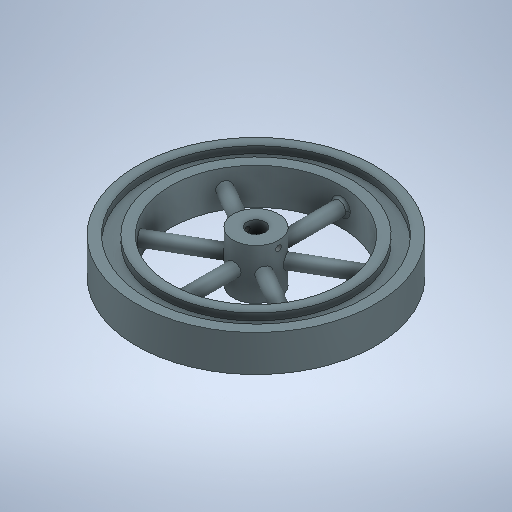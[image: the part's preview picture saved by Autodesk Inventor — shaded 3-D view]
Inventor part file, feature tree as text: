
AUTODESK INVENTOR PART (.ipt)
format: ipt  version: 2025.1 (Build 291241000, 241)  size: 387,072 bytes
history: native  units: mm
features: sketch x7, extrude x5, plane x3, hole x2, mirror x1, fillet x1, pattern_circular x1
ambient origin geometry x8: Origin, YZ Plane, XZ Plane, XY Plane, X Axis, Y Axis, Z Axis, Center Point
bodies: Solid1 (feature_tree)
feature tree (20):
  extrude  "Extrusion1"  Depth=16.0mm TaperAngle=0.0deg
  extrude  "Extrusion2"  Depth=16.0mm TaperAngle=0.0deg
  extrude  "Extrusion3"  Depth=96.0mm
  plane  "Work Plane1"
  mirror  "Mirror1"
  extrude  "Extrusion4"  TaperAngle=0.0deg  [1 undecoded]
  plane  "Work Plane2"
  extrude  "Extrusion5"  Depth=9.5mm TaperAngle=0.0deg
  fillet  "Fillet1"  Radius=9.5mm
  pattern_circular  "Circular Pattern1"  [2 undecoded]
  plane  "Work Plane3"
  hole  "Hole2"  [1 undecoded]
  hole  "Hole3"  [1 undecoded]
  sketch  "Sketch1"  dims[d0=105.0mm d1=16.0mm d2=0.0mm]
  sketch  "Sketch2"  dims[d3=75.0mm d4=16.0mm d5=0.0mm]
  sketch  "Sketch3"  dims[d6=84.0mm d7=96.0mm]
  sketch  "Sketch4"  dims[d8=3.0mm d9=0.0mm d10=0.0mm]
  sketch  "Sketch6"  dims[d11=20.0mm d12=22.0mm d13=0.0mm d21=9.5mm]
  sketch  "Sketch7"  dims[d22=6.0mm]
  sketch  "Sketch8"  dims[d23=18.0mm d24=0.0mm d25=1.0mm d26=60.0mm d27=360.0deg d29=10.0mm d30=8.0mm d31=2.459mm d32=20.0mm d33=4.0mm d34=2.0mm d35=90.0deg d36=20.0mm d37=0.0mm d38=8.0mm d39=20.0mm d40=4.0mm d41=2.0mm d42=90.0deg d43=20.0mm d44=0.0mm]
note: 5 required parameter values undecoded (feature->parameter linkage not recoverable at this tier; creation-order binding heuristic only, values carry confidence <= 0.55)
